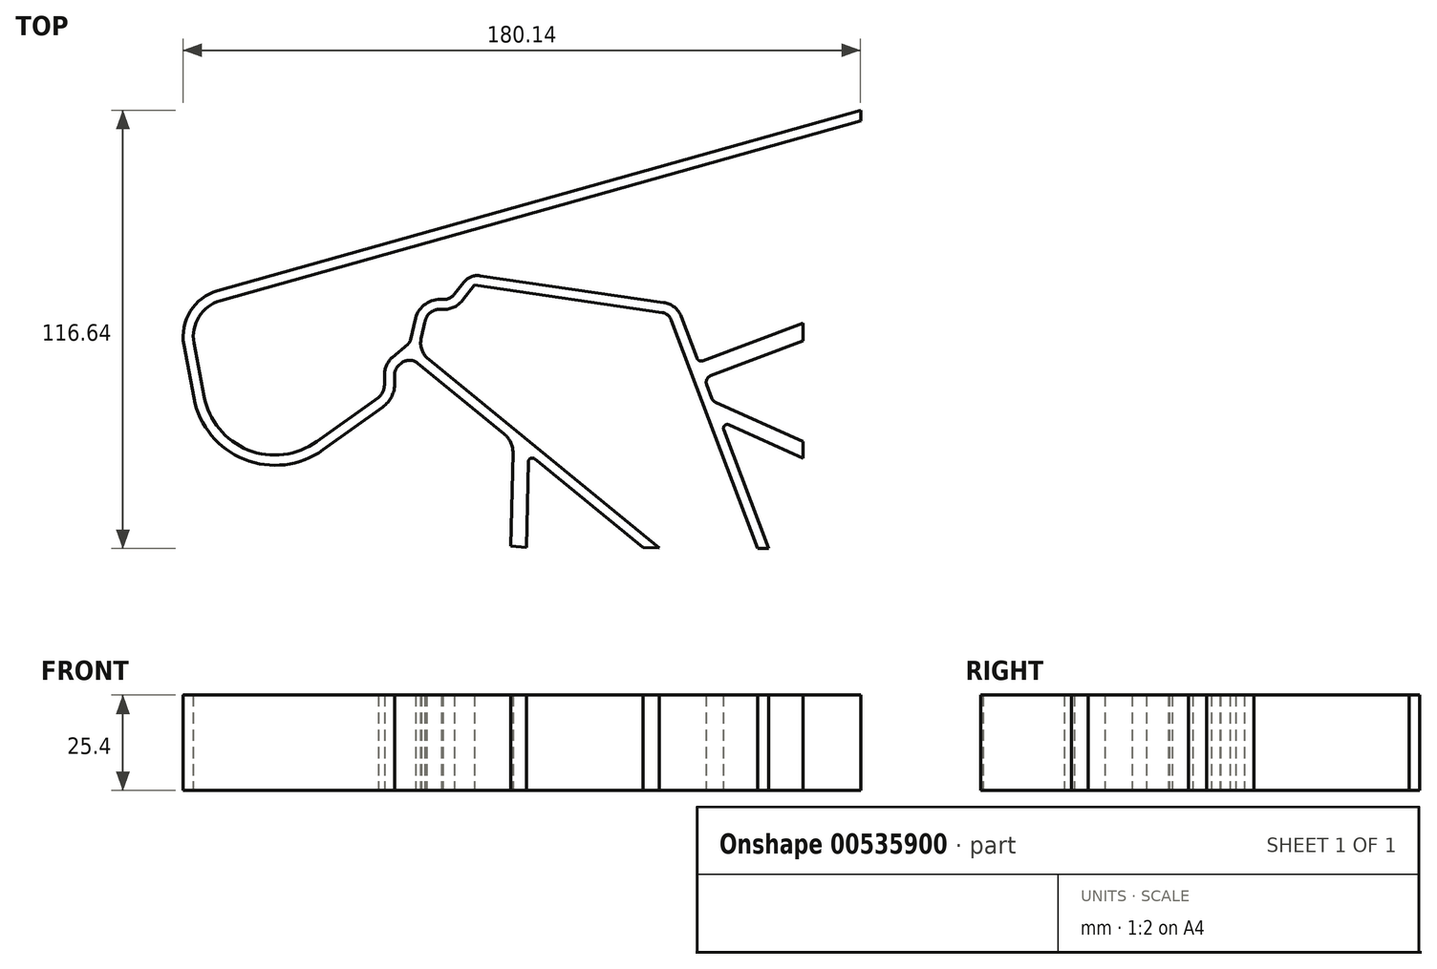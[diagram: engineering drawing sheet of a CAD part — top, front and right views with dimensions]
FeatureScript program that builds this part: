
annotation { "Feature Type Name" : "Feature", "Feature Type Description" : "" }
export const myFeature = defineFeature(function(context is Context, id is Id, definition is map)
    precondition{}
    {
        {
            var Q0;
            Q0=qCreatedBy(makeId("Top.planeOp"),FACE);
            var sketch = newSketch(context, id + "F0", { "sketchPlane" : qUnion([Q0])});
            skLineSegment(sketch, "E0", {"start": v(-138.12, -4.48) * mm, "end": v(-138.12, -9.29) * mm});
            skPoint(sketch, "E1.visualSharp", {"position": v(-303.25, 0) * mm});
            skPoint(sketch, "E2.visualSharp", {"position": v(-292.69, -55.93) * mm});
            skPoint(sketch, "E3.visualSharp", {"position": v(-247.95, -23.79) * mm});
            skPoint(sketch, "E4.visualSharp", {"position": v(-215.77, -33.7) * mm});
            skPoint(sketch, "E5.visualSharp", {"position": v(-242.79, -11.59) * mm});
            skPoint(sketch, "E6.visualSharp", {"position": v(-248.04, -16.1) * mm});
            skPoint(sketch, "E7.visualSharp", {"position": v(-238.68, 1.2) * mm});
            skPoint(sketch, "E8.visualSharp", {"position": v(-231.6, 0) * mm});
            skPoint(sketch, "E9.visualSharp", {"position": v(-226.05, 7.03) * mm});
            skPoint(sketch, "E10.visualSharp", {"position": v(-166.7, -16.7) * mm});
            skPoint(sketch, "E11.visualSharp", {"position": v(-163.1, -26.26) * mm});
            skLineSegment(sketch, "E12.0", {"start": v(-246.63, -20.47) * mm, "end": v(-246.66, -18.3) * mm});
            skArc(sketch, "E12.1", {"start": v(-249.84, -26.82) * mm, "mid": v(-247.46, -24.04) * mm, "end": v(-246.63, -20.47) * mm});
            skLineSegment(sketch, "E12.2", {"start": v(-265.73, -38.24) * mm, "end": v(-249.84, -26.82) * mm});
            skLineSegment(sketch, "E12.3", {"start": v(-122.76, 52.14) * mm, "end": v(-293.72, 4.1) * mm});
            skArc(sketch, "E12.4", {"start": v(-293.72, 4.1) * mm, "mid": v(-301, -1.4) * mm, "end": v(-302.68, -10.36) * mm});
            skLineSegment(sketch, "E12.5", {"start": v(-302.68, -10.36) * mm, "end": v(-300, -24.53) * mm});
            skArc(sketch, "E12.6", {"start": v(-300, -24.53) * mm, "mid": v(-286.63, -40.79) * mm, "end": v(-265.73, -38.24) * mm});
            skLineSegment(sketch, "E13.0", {"start": v(-122.76, 49.32) * mm, "end": v(-292.98, 1.48) * mm});
            skArc(sketch, "E13.1", {"start": v(-292.98, 1.48) * mm, "mid": v(-298.7, -2.82) * mm, "end": v(-300, -9.86) * mm});
            skLineSegment(sketch, "E13.2", {"start": v(-247.25, -13.64) * mm, "end": v(-243.1, -10.06) * mm});
            skArc(sketch, "E13.3", {"start": v(-243.1, -10.06) * mm, "mid": v(-242.73, -9.63) * mm, "end": v(-242.51, -9.1) * mm});
            skLineSegment(sketch, "E13.4", {"start": v(-242.51, -9.1) * mm, "end": v(-241.11, -3.18) * mm});
            skArc(sketch, "E13.5", {"start": v(-233.85, 1.76) * mm, "mid": v(-238.37, 0.6) * mm, "end": v(-241.11, -3.18) * mm});
            skArc(sketch, "E13.6", {"start": v(-247.25, -13.64) * mm, "mid": v(-248.83, -15.75) * mm, "end": v(-249.37, -18.34) * mm});
            skLineSegment(sketch, "E13.7", {"start": v(-249.35, -20.5) * mm, "end": v(-249.37, -18.34) * mm});
            skArc(sketch, "E13.8", {"start": v(-250.9, -24.3) * mm, "mid": v(-249.72, -22.57) * mm, "end": v(-249.35, -20.5) * mm});
            skLineSegment(sketch, "E13.9", {"start": v(-267.32, -36.03) * mm, "end": v(-250.9, -24.3) * mm});
            skArc(sketch, "E13.10", {"start": v(-297.33, -24.03) * mm, "mid": v(-285.62, -38.26) * mm, "end": v(-267.32, -36.03) * mm});
            skLineSegment(sketch, "E13.11", {"start": v(-300, -9.86) * mm, "end": v(-297.33, -24.03) * mm});
            skLineSegment(sketch, "E14.0", {"start": v(-173.06, -3.73) * mm, "end": v(-150.1, -64.48) * mm});
            skArc(sketch, "E14.1", {"start": v(-234.23, -0.9) * mm, "mid": v(-231.15, -0.38) * mm, "end": v(-228.67, 1.52) * mm});
            skLineSegment(sketch, "E14.2", {"start": v(-228.67, 1.52) * mm, "end": v(-225.47, 5.57) * mm});
            skLineSegment(sketch, "E14.3", {"start": v(-225.47, 5.57) * mm, "end": v(-175.57, -1.7) * mm});
            skArc(sketch, "E14.4", {"start": v(-173.06, -3.73) * mm, "mid": v(-174.04, -2.37) * mm, "end": v(-175.57, -1.7) * mm});
            skLineSegment(sketch, "E15.0", {"start": v(-164.75, -14.54) * mm, "end": v(-138.12, -4.48) * mm});
            skArc(sketch, "E15.1", {"start": v(-166.27, -13.85) * mm, "mid": v(-165.65, -14.51) * mm, "end": v(-164.75, -14.54) * mm});
            skLineSegment(sketch, "E15.2", {"start": v(-170.46, -2.77) * mm, "end": v(-166.27, -13.85) * mm});
            skArc(sketch, "E15.3", {"start": v(-170.46, -2.77) * mm, "mid": v(-172.28, -0.26) * mm, "end": v(-175.12, 0.98) * mm});
            skArc(sketch, "E15.4", {"start": v(-233.85, 1.76) * mm, "mid": v(-232.12, 2.1) * mm, "end": v(-230.74, 3.2) * mm});
            skLineSegment(sketch, "E15.5", {"start": v(-230.74, 3.2) * mm, "end": v(-228.19, 6.43) * mm});
            skArc(sketch, "E15.6", {"start": v(-223.98, 8.1) * mm, "mid": v(-226.3, 7.83) * mm, "end": v(-228.19, 6.43) * mm});
            skLineSegment(sketch, "E15.7", {"start": v(-223.98, 8.1) * mm, "end": v(-175.12, 0.98) * mm});
            skArc(sketch, "E16.0", {"start": v(-245.48, -15.7) * mm, "mid": v(-246.36, -16.87) * mm, "end": v(-246.66, -18.3) * mm});
            skArc(sketch, "E16.1", {"start": v(-234.23, -0.9) * mm, "mid": v(-237.15, -1.67) * mm, "end": v(-238.6, -4.33) * mm});
            skLineSegment(sketch, "E16.2", {"start": v(-239.51, -8.22) * mm, "end": v(-238.6, -4.33) * mm});
            skLineSegment(sketch, "E16.4", {"start": v(-245.48, -15.7) * mm, "end": v(-244.92, -15.22) * mm});
            skLineSegment(sketch, "E17.0", {"start": v(-162.65, -18.56) * mm, "end": v(-138.12, -9.29) * mm});
            skLineSegment(sketch, "E18.0", {"start": v(-157.78, -31.58) * mm, "end": v(-138.12, -40.45) * mm});
            skLineSegment(sketch, "E19.0", {"start": v(-159.15, -32.86) * mm, "end": v(-147.2, -64.5) * mm});
            skLineSegment(sketch, "E20.0", {"start": v(-161.34, -25.56) * mm, "end": v(-138.12, -36.04) * mm});
            skArc(sketch, "E20.1", {"start": v(-162.29, -24.55) * mm, "mid": v(-161.91, -25.15) * mm, "end": v(-161.34, -25.56) * mm});
            skLineSegment(sketch, "E21.1", {"start": v(-238.08, -13.68) * mm, "end": v(-176.25, -64.3) * mm});
            skLineSegment(sketch, "E22.0", {"start": v(-215.2, -39.08) * mm, "end": v(-215.76, -63.87) * mm});
            skArc(sketch, "E23.0", {"start": v(-240.56, -15.16) * mm, "mid": v(-242.75, -14.4) * mm, "end": v(-244.92, -15.22) * mm});
            skLineSegment(sketch, "E24.0", {"start": v(-211.1, -41.4) * mm, "end": v(-211.61, -64.26) * mm});
            skLineSegment(sketch, "E25.0", {"start": v(-209.44, -40.64) * mm, "end": v(-180.18, -64.6) * mm});
            skLineSegment(sketch, "E26", {"start": v(-240.56, -15.16) * mm, "end": v(-217.53, -34.02) * mm});
            skArc(sketch, "E27.filletArc", {"start": v(-209.44, -40.64) * mm, "mid": v(-210.5, -40.5) * mm, "end": v(-211.1, -41.4) * mm});
            skPoint(sketch, "E28.visualSharp", {"position": v(-215.13, -35.98) * mm});
            skArc(sketch, "E28.filletArc", {"start": v(-215.2, -39.08) * mm, "mid": v(-215.78, -36.28) * mm, "end": v(-217.53, -34.02) * mm});
            skArc(sketch, "E29", {"start": v(-239.51, -8.22) * mm, "mid": v(-239.56, -11.15) * mm, "end": v(-238.08, -13.68) * mm});
            skPoint(sketch, "E29.first.point", {"position": v(-239.51, -8.22) * mm});
            skPoint(sketch, "E29.second.point", {"position": v(-237.41, -14.23) * mm});
            skPoint(sketch, "E29.third.point", {"position": v(-230.73, -5.74) * mm});
            skLineSegment(sketch, "E30.filletArc", {"start": v(-164.32, -19.19) * mm, "end": v(-164.32, -19.19) * mm});
            skArc(sketch, "E31.filletArc", {"start": v(-162.65, -18.56) * mm, "mid": v(-163.64, -19.49) * mm, "end": v(-163.69, -20.85) * mm});
            skArc(sketch, "E32.filletArc", {"start": v(-157.78, -31.58) * mm, "mid": v(-158.9, -31.76) * mm, "end": v(-159.15, -32.86) * mm});
            skLineSegment(sketch, "E33", {"start": v(-162.29, -24.55) * mm, "end": v(-163.69, -20.85) * mm});
            skLineSegment(sketch, "E34", {"start": v(-122.76, 52.14) * mm, "end": v(-122.76, 49.32) * mm});
            skPoint(sketch, "E35.orphan", {"position": v(-122.76, 58.95) * mm});
            skLineSegment(sketch, "E36.trimOffspring", {"start": v(-138.12, -36.04) * mm, "end": v(-138.12, -40.45) * mm});
            skPoint(sketch, "E37.orphan", {"position": v(-133.48, -64.6) * mm});
            skLineSegment(sketch, "E38.trimOffspring", {"start": v(-150.1, -64.48) * mm, "end": v(-147.2, -64.5) * mm});
            skLineSegment(sketch, "E39.trimOffspring", {"start": v(-180.58, -64.26) * mm, "end": v(-176.25, -64.3) * mm});
            skPoint(sketch, "E40.start.orphan", {"position": v(-237.22, -63.87) * mm});
            skLineSegment(sketch, "E41", {"start": v(-215.76, -63.87) * mm, "end": v(-211.61, -64.26) * mm});
            skSolve(sketch);
        }
        {
            var Q0;
            Q0 = qSketchRegion(id + "F0", true);
            extrude(context, id + "F1", {"entities" : qUnion([Q0]), "depth" : 25.4 * mm, "offsetDistance" : 25.4 * mm});
        }
    });
